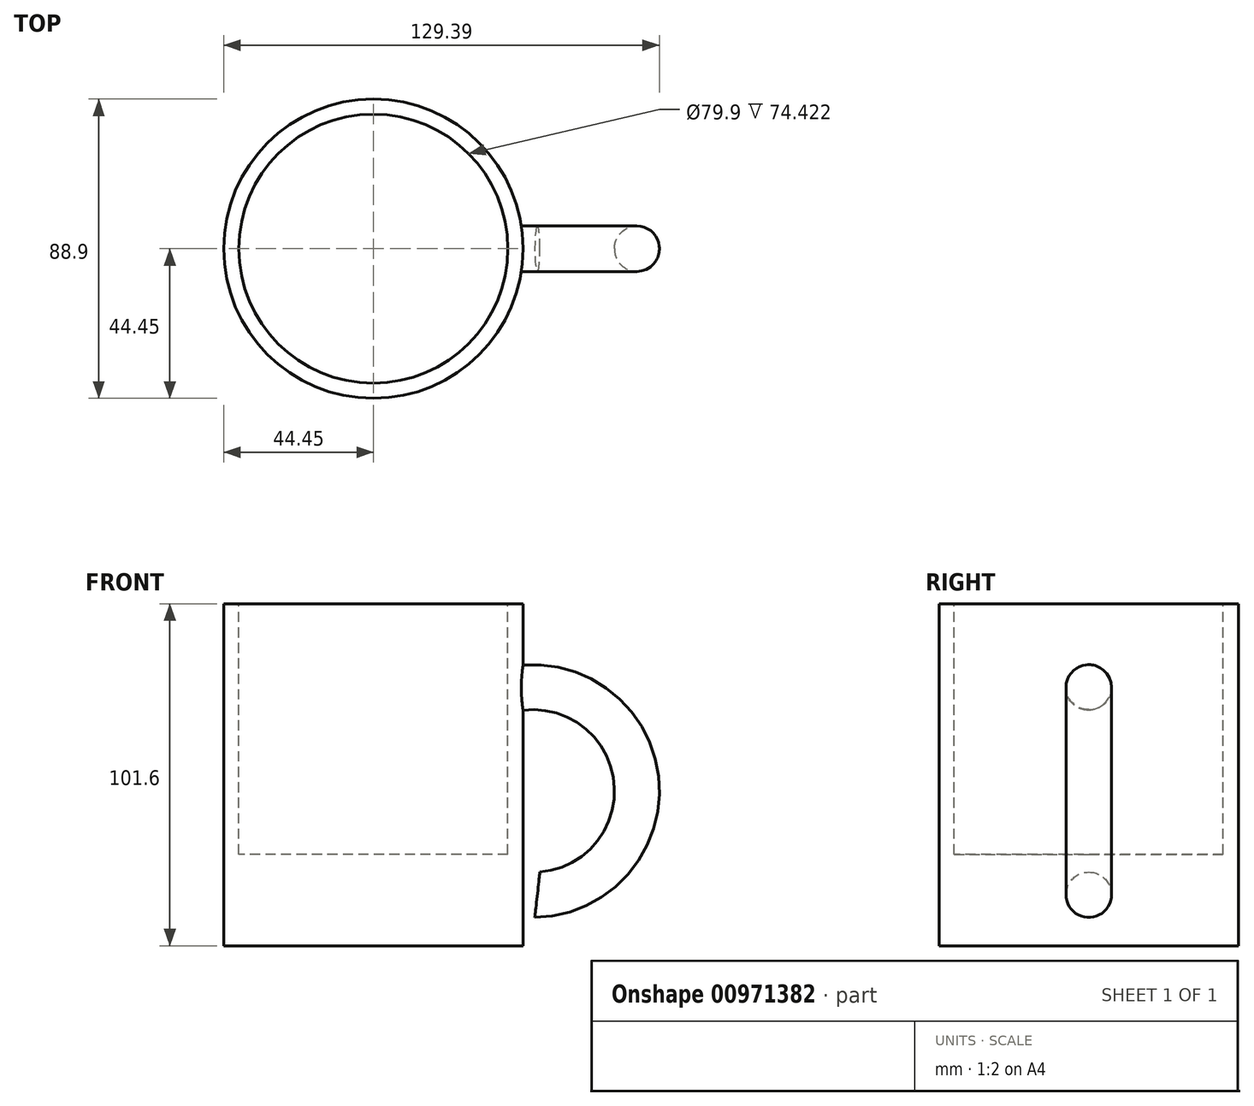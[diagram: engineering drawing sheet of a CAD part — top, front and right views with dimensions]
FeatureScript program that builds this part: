
annotation { "Feature Type Name" : "Feature", "Feature Type Description" : "" }
export const myFeature = defineFeature(function(context is Context, id is Id, definition is map)
    precondition{}
    {
        {
            var Q0;
            Q0=qCreatedBy(makeId("Top.planeOp"),FACE);
            var sketch = newSketch(context, id + "F0", { "sketchPlane" : qUnion([Q0])});
            skCircle(sketch, "E0", {"center": v(0, 0) * mm, "radius": 44.45 * mm});
            skSolve(sketch);
        }
        {
            var Q0;
            Q0=makeQuery(id+"F0.imprint","IMPRINT",FACE,{"disambiguationData":[TD([[makeQuery(id+"F0.imprint","IMPRINT",EDGE,{"derivedFrom":sQuery(id+"F0.wireOp",EDGE,"E0")}),1.0]])]});
            extrude(context, id + "F1", {"entities" : qUnion([Q0]), "depth" : 101.6 * mm, "offsetDistance" : 25.4 * mm});
        }
        {
            var Q0;
            Q0=qCreatedBy(makeId("Front.planeOp"),FACE);
            var sketch = newSketch(context, id + "F2", { "sketchPlane" : qUnion([Q0])});
            skArc(sketch, "E1", {"start": v(45.51, 15.18) * mm, "mid": v(78.25, 45.8) * mm, "end": v(45.84, 76.75) * mm});
            skSolve(sketch);
        }
        {
            var Q0;
            Q0=qCreatedBy(makeId("Right.planeOp"),FACE);
            cPlane(context, id + "F3", {"entities" : qUnion([Q0]), "cplaneType" : CPlaneType.OFFSET, "offset" : 42.67 * mm, "width" : 152.4 * mm, "height" : 152.4 * mm});
        }
        {
            var Q0;
            Q0=qCreatedBy(id+"F3.planeOp",FACE);
            var sketch = newSketch(context, id + "F4", { "sketchPlane" : qUnion([Q0])});
            skCircle(sketch, "E2", {"center": v(0, 76.42) * mm, "radius": 6.76 * mm});
            skSolve(sketch);
        }
        {
            var Q0;
            Q0 = qSketchRegion(id + "F4", true);
            var Q1;
            Q1 = qConstructionFilter(qBodyType(qCreatedBy(id + "F2" ,EDGE), BodyType.WIRE), ConstructionObject.NO);
            sweep(context, id + "F5", {"operationType" : NewBodyOperationType.ADD, "profiles" : qUnion([Q0]), "path" : qUnion([Q1])});
        }
        {
            var Q0;
            Q0=makeQuery(id+"F1.opExtrude","CAP_FACE",FACE,{"disambiguationData":[OSD([sQuery(id+"F0.wireOp",EDGE,"E0")])],"isStart":false});
            var sketch = newSketch(context, id + "F6", { "sketchPlane" : qUnion([Q0])});
            skCircle(sketch, "E3", {"center": v(0, 0) * mm, "radius": 39.95 * mm});
            skSolve(sketch);
        }
        {
            var Q0;
            Q0=makeQuery(id+"F6.imprint","IMPRINT",FACE,{"disambiguationData":[TD([[makeQuery(id+"F6.imprint","IMPRINT",EDGE,{"derivedFrom":sQuery(id+"F6.wireOp",EDGE,"E3")}),1.0]])]});
            extrude(context, id + "F7", {"entities" : qUnion([Q0]), "operationType" : NewBodyOperationType.REMOVE, "oppositeDirection" : true, "depth" : 74.42 * mm, "offsetDistance" : 25.4 * mm});
        }
    });
